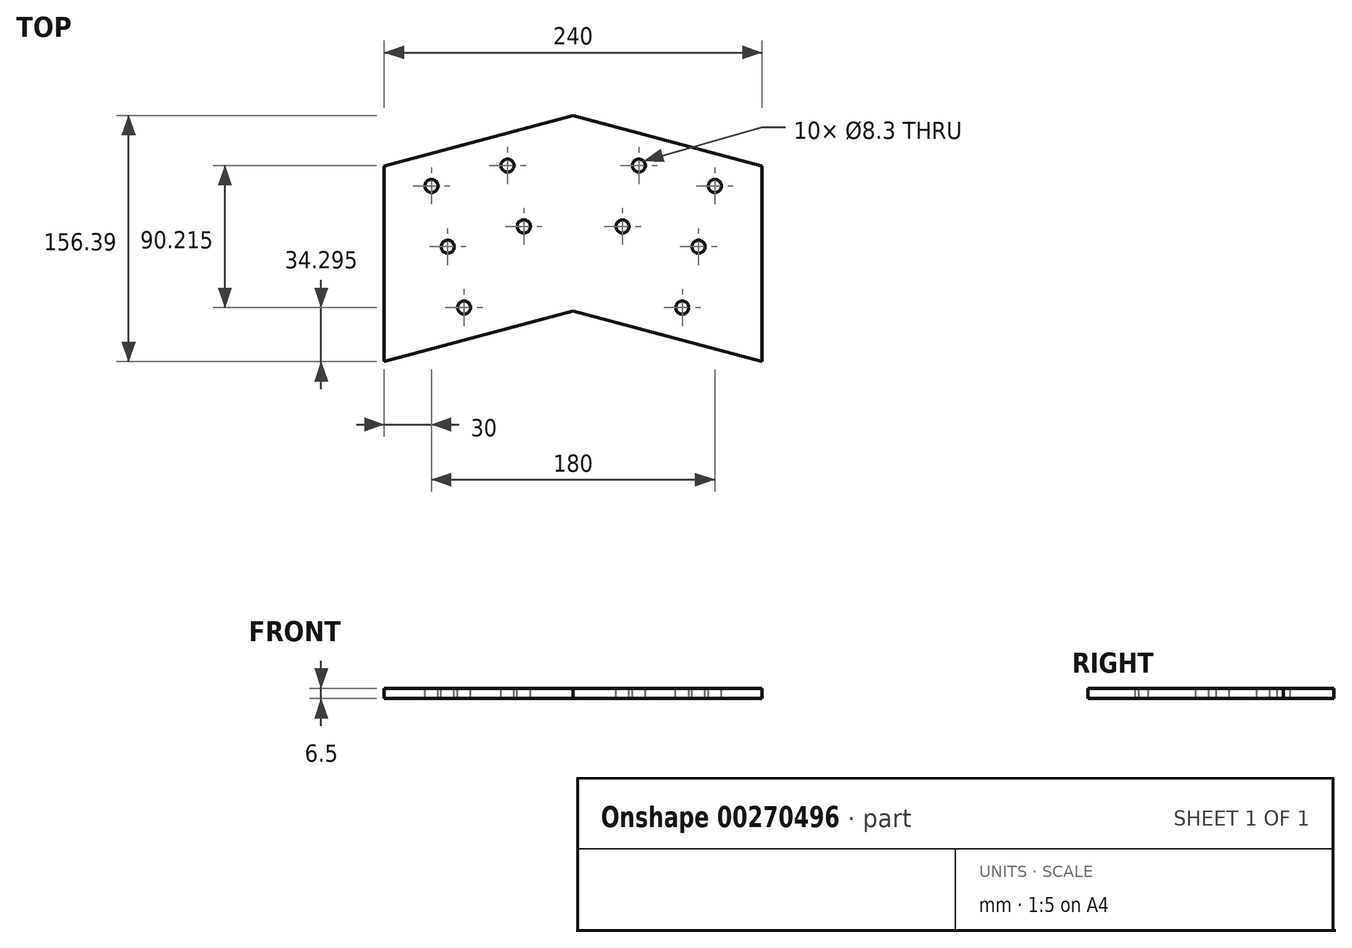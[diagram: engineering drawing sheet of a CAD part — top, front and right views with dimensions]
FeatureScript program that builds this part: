
annotation { "Feature Type Name" : "Feature", "Feature Type Description" : "" }
export const myFeature = defineFeature(function(context is Context, id is Id, definition is map)
    precondition{}
    {
        {
            var Q0;
            Q0=qCreatedBy(makeId("Top.planeOp"),FACE);
            var sketch = newSketch(context, id + "F0", { "sketchPlane" : qUnion([Q0])});
            skLineSegment(sketch, "E0", {"start": v(0, 0) * mm, "end": v(-120, -32.15) * mm});
            skLineSegment(sketch, "E1", {"start": v(-120, -32.15) * mm, "end": v(-120, -156.39) * mm});
            skLineSegment(sketch, "E2", {"start": v(-120, -156.39) * mm, "end": v(0, -124.23) * mm});
            skLineSegment(sketch, "E3", {"start": v(0, -124.23) * mm, "end": v(120, -156.39) * mm});
            skLineSegment(sketch, "E4", {"start": v(120, -156.39) * mm, "end": v(120, -32.15) * mm});
            skLineSegment(sketch, "E5", {"start": v(120, -32.15) * mm, "end": v(0, 0) * mm});
            skSolve(sketch);
        }
        {
            var Q0;
            Q0=makeQuery(id+"F0.imprint","IMPRINT",FACE,{"disambiguationData":[TD([[makeQuery(id+"F0.imprint","IMPRINT",EDGE,{"derivedFrom":sQuery(id+"F0.wireOp",EDGE,"E0")}),1.0]])]});
            extrude(context, id + "F1", {"entities" : qUnion([Q0]), "depth" : 6.5 * mm});
        }
        {
            var Q0;
            Q0=makeQuery(id+"F1.opExtrude","CAP_FACE",FACE,{"disambiguationData":[OSD([sQuery(id+"F0.wireOp",EDGE,"E0"),sQuery(id+"F0.wireOp",EDGE,"E1"),sQuery(id+"F0.wireOp",EDGE,"E2"),sQuery(id+"F0.wireOp",EDGE,"E3"),sQuery(id+"F0.wireOp",EDGE,"E4"),sQuery(id+"F0.wireOp",EDGE,"E5")])],"isStart":false});
            var sketch = newSketch(context, id + "F2", { "sketchPlane" : qUnion([Q0])});
            skLineSegment(sketch, "E6.0", {"start": v(3.88, -19.67) * mm, "end": v(-191.12, -71.92) * mm, "construction": true});
            skLineSegment(sketch, "E7.0", {"start": v(191.12, -71.92) * mm, "end": v(-3.88, -19.67) * mm, "construction": true});
            skLineSegment(sketch, "E8.0", {"start": v(14.24, -58.3) * mm, "end": v(-180.76, -110.55) * mm, "construction": true});
            skLineSegment(sketch, "E9.0", {"start": v(8.64, -101.21) * mm, "end": v(-170.41, -149.19) * mm, "construction": true});
            skLineSegment(sketch, "E10.0", {"start": v(180.76, -110.55) * mm, "end": v(-14.24, -58.3) * mm, "construction": true});
            skLineSegment(sketch, "E11.0", {"start": v(170.41, -149.19) * mm, "end": v(-11.38, -100.48) * mm, "construction": true});
            skPoint(sketch, "E12", {"position": v(-90, -44.82) * mm});
            skLineSegment(sketch, "E13", {"start": v(-90, -44.82) * mm, "end": v(-61.12, -152.6) * mm, "construction": true});
            skPoint(sketch, "E14", {"position": v(90, -44.82) * mm});
            skLineSegment(sketch, "E15", {"start": v(90, -44.82) * mm, "end": v(61.77, -150.16) * mm, "construction": true});
            skLineSegment(sketch, "E16", {"start": v(-41.7, -31.88) * mm, "end": v(-11.52, -144.53) * mm, "construction": true});
            skPoint(sketch, "E17", {"position": v(-31.35, -70.52) * mm});
            skPoint(sketch, "E18", {"position": v(-79.65, -83.46) * mm});
            skPoint(sketch, "E19", {"position": v(-69.3, -122.1) * mm});
            skLineSegment(sketch, "E20", {"start": v(41.7, -31.88) * mm, "end": v(11.9, -143.11) * mm, "construction": true});
            skPoint(sketch, "E21", {"position": v(31.35, -70.52) * mm});
            skPoint(sketch, "E22", {"position": v(79.65, -83.46) * mm});
            skPoint(sketch, "E23", {"position": v(69.3, -122.1) * mm});
            skSolve(sketch);
        }
        {
            var Q0;
            Q0=sQuery(id+"F2.wireOp",VERTEX,"E12");
            var Q1;
            Q1=sQuery(id+"F2.wireOp",VERTEX,"E16.start");
            var Q2;
            Q2=sQuery(id+"F2.wireOp",VERTEX,"E18");
            var Q3;
            Q3=sQuery(id+"F2.wireOp",VERTEX,"E17");
            var Q4;
            Q4=sQuery(id+"F2.wireOp",VERTEX,"E19");
            var Q5;
            Q5=sQuery(id+"F2.wireOp",VERTEX,"E20.start");
            var Q6;
            Q6=sQuery(id+"F2.wireOp",VERTEX,"E14");
            var Q7;
            Q7=sQuery(id+"F2.wireOp",VERTEX,"E22");
            var Q8;
            Q8=sQuery(id+"F2.wireOp",VERTEX,"E23");
            var Q9;
            Q9=sQuery(id+"F2.wireOp",VERTEX,"E21");
            var Q10;
            Q10=makeQuery(id+"F1.opExtrude","SWEPT_BODY",BODY,{"disambiguationData":[OSD([sQuery(id+"F0.wireOp",EDGE,"E0"),sQuery(id+"F0.wireOp",EDGE,"E1"),sQuery(id+"F0.wireOp",EDGE,"E2"),sQuery(id+"F0.wireOp",EDGE,"E3"),sQuery(id+"F0.wireOp",EDGE,"E4"),sQuery(id+"F0.wireOp",EDGE,"E5")])]});
            hole(context, id + "F3", {"style" : HoleStyle.SIMPLE, "endStyle" : HoleEndStyle.THROUGH, "standardTappedOrClearance" : lookupTablePath({ "standard" : "ISO", "size" : "8.3", "type" : "Drilled" }), "standardBlindInLast" : lookupTablePath({ "standard" : "ISO", "size" : "8.3", "type" : "Drilled" }), "holeDiameter" : 8.3 * mm, "tappedDepth" : 12 * mm, "tapClearance" : 3, "locations" : qUnion([Q0, Q1, Q2, Q3, Q4, Q5, Q6, Q7, Q8, Q9]), "scope" : qUnion([Q10])});
        }
    });
